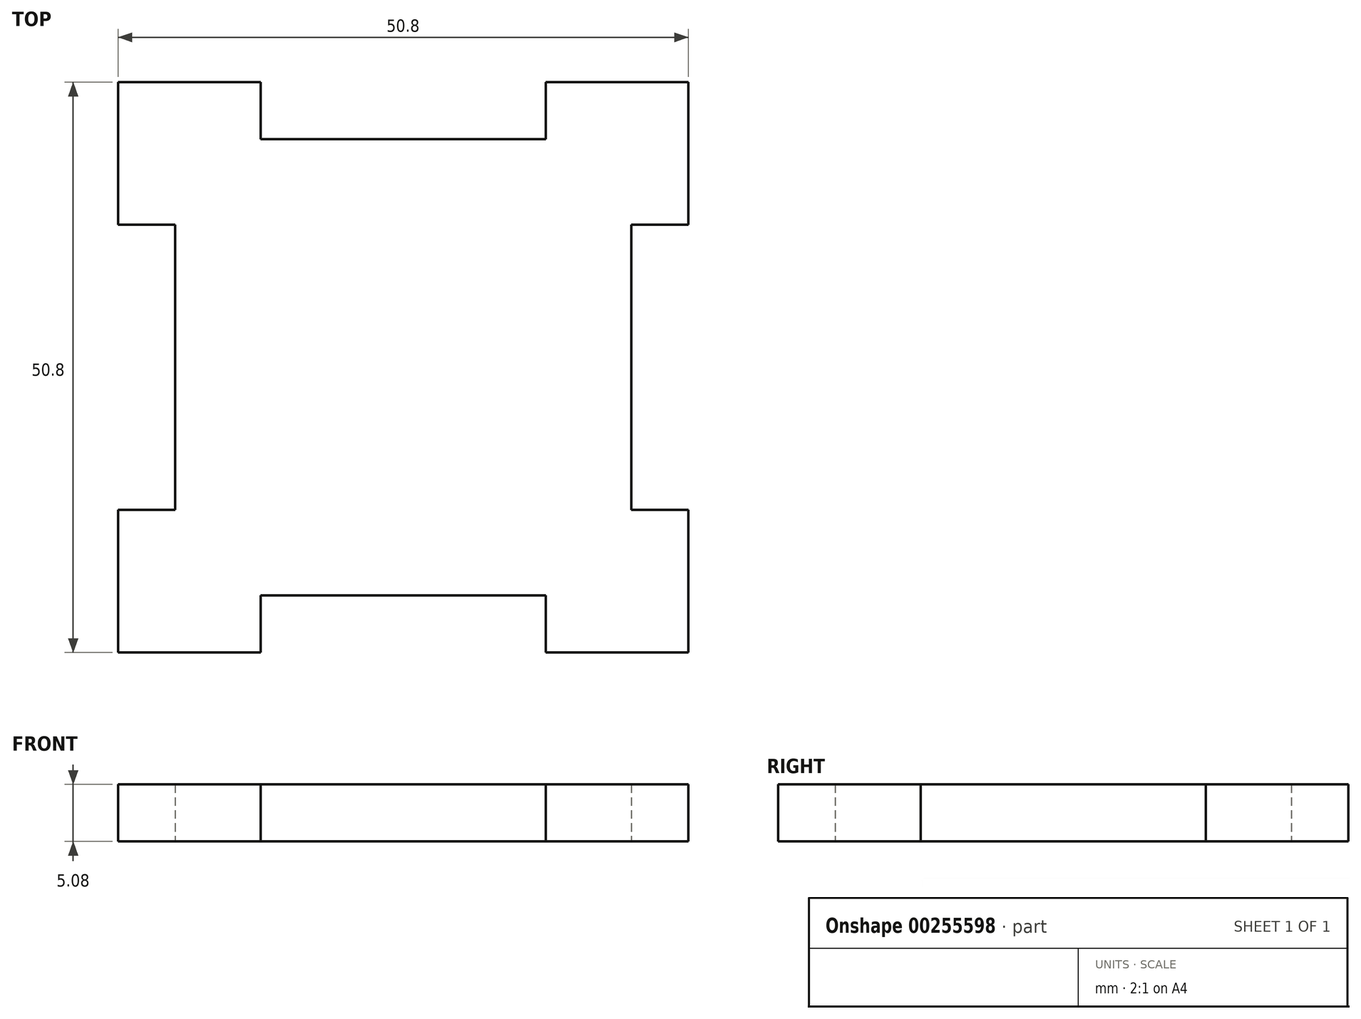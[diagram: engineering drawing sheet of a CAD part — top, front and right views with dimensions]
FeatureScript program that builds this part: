
annotation { "Feature Type Name" : "Feature", "Feature Type Description" : "" }
export const myFeature = defineFeature(function(context is Context, id is Id, definition is map)
    precondition{}
    {
        {
            var Q0;
            Q0=qCreatedBy(makeId("Top.planeOp"),FACE);
            var sketch = newSketch(context, id + "F0", { "sketchPlane" : qUnion([Q0])});
            skLineSegment(sketch, "E0.bottom", {"start": v(0, 0) * mm, "end": v(-12.7, 0) * mm});
            skLineSegment(sketch, "E0.top", {"start": v(0, 50.8) * mm, "end": v(-12.7, 50.8) * mm});
            skLineSegment(sketch, "E0.left", {"start": v(0, 0) * mm, "end": v(0, 12.7) * mm});
            skLineSegment(sketch, "E0.right", {"start": v(-50.8, 0) * mm, "end": v(-50.8, 12.7) * mm});
            skLineSegment(sketch, "E1.bottom", {"start": v(-50.8, 38.1) * mm, "end": v(-45.72, 38.1) * mm});
            skLineSegment(sketch, "E1.top", {"start": v(-50.8, 12.7) * mm, "end": v(-45.72, 12.7) * mm});
            skLineSegment(sketch, "E1.right", {"start": v(-45.72, 38.1) * mm, "end": v(-45.72, 12.7) * mm});
            skLineSegment(sketch, "E2.top", {"start": v(-38.1, 5.08) * mm, "end": v(-12.7, 5.08) * mm});
            skLineSegment(sketch, "E2.left", {"start": v(-38.1, 0) * mm, "end": v(-38.1, 5.08) * mm});
            skLineSegment(sketch, "E2.right", {"start": v(-12.7, 0) * mm, "end": v(-12.7, 5.08) * mm});
            skLineSegment(sketch, "E3.bottom", {"start": v(0, 12.7) * mm, "end": v(-5.08, 12.7) * mm});
            skLineSegment(sketch, "E3.top", {"start": v(0, 38.1) * mm, "end": v(-5.08, 38.1) * mm});
            skLineSegment(sketch, "E3.right", {"start": v(-5.08, 12.7) * mm, "end": v(-5.08, 38.1) * mm});
            skLineSegment(sketch, "E4.top", {"start": v(-38.1, 45.72) * mm, "end": v(-12.7, 45.72) * mm});
            skLineSegment(sketch, "E4.left", {"start": v(-38.1, 50.8) * mm, "end": v(-38.1, 45.72) * mm});
            skLineSegment(sketch, "E4.right", {"start": v(-12.7, 50.8) * mm, "end": v(-12.7, 45.72) * mm});
            skLineSegment(sketch, "E5.trimOffspring", {"start": v(-50.8, 38.1) * mm, "end": v(-50.8, 50.8) * mm});
            skLineSegment(sketch, "E6.trimOffspring", {"start": v(-38.1, 50.8) * mm, "end": v(-50.8, 50.8) * mm});
            skLineSegment(sketch, "E7.trimOffspring", {"start": v(0, 38.1) * mm, "end": v(0, 50.8) * mm});
            skLineSegment(sketch, "E8.trimOffspring", {"start": v(-38.1, 0) * mm, "end": v(-50.8, 0) * mm});
            skSolve(sketch);
        }
        {
            var Q0;
            Q0=makeQuery(id+"F0.imprint","IMPRINT",FACE,{"disambiguationData":[TD([[makeQuery(id+"F0.imprint","IMPRINT",EDGE,{"derivedFrom":sQuery(id+"F0.wireOp",EDGE,"E0.bottom")}),-1.0]])]});
            extrude(context, id + "F1", {"entities" : qUnion([Q0]), "depth" : 5.08 * mm});
        }
    });
